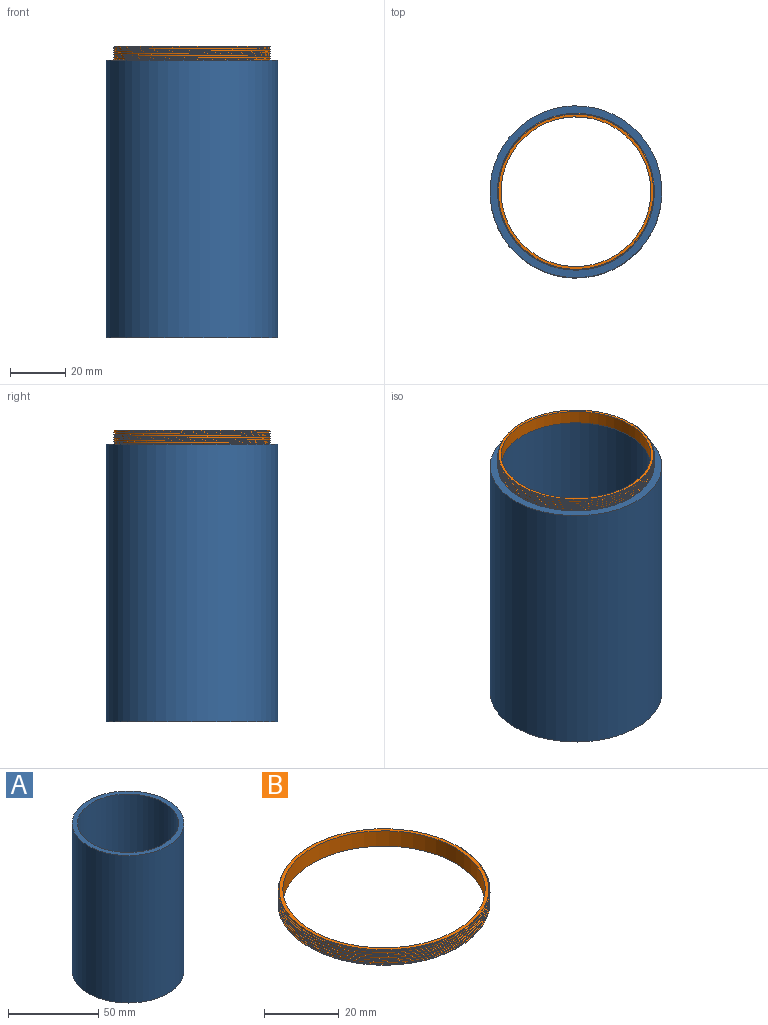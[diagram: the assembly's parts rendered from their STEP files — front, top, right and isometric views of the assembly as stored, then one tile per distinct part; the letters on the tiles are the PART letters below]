
ASSEMBLY  parts=2 mates=1
PART A: 4 faces, bbox 62x62x100 mm
  f0: cylinder r=28mm len=100mm, axis (0,0,-1), area 17592.9mm2, adj f2,f3
  f1: cylinder r=31mm len=100mm, axis (0,0,-1), area 19477.9mm2, adj f2,f3
  f2: plane 62x62mm, normal (0,0,1), area 556.1mm2, adj f0,f1
  f3: plane 62x62mm, normal (0,0,-1), area 556.1mm2, adj f0,f1
PART B: 9 faces, bbox 56.5x65.3x5.3 mm
  f0: cylinder r=27mm len=54mm, axis (0,0,-1), area 848.2mm2, adj f2,f3
  f1: cylinder r=28mm len=56mm, axis (0,0,-1), area 615.6mm2, adj f2,f3,f4,f6,f8
  f2: plane 56x56mm, normal (0,0,1), area 172.8mm2, adj f0,f1
  f3: plane 56x56mm, normal (0,0,-1), area 172.8mm2, adj f0,f1,f7
  f4: plane 0.27x0.26mm, normal (0,1,0), area 0mm2, adj f1,f6,f8
  f5: plane 0.27x0.26mm, normal (0,-1,0), area 0mm2, adj f6,f7,f8
  f6: bspline ~65.29x56.54mm, area 318.3mm2, adj f1,f4,f5,f8
  f7: cylinder r=28mm len=39.24mm, axis (0,0,-1), area 7.4mm2, adj f3,f5,f8
  f8: bspline ~65.29x56.54mm, area 318.3mm2, adj f1,f4,f5,f6,f7
PLACE A t=(-62.08,6.68,-19.32)mm
PLACE B t=(-139.57,6.68,80.68)mm
MATE fastened B.f0 <-> A.f0  axis (0,0,-1) through (-62.08,6.68,80.68)mm
